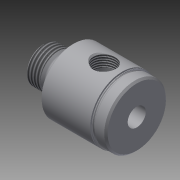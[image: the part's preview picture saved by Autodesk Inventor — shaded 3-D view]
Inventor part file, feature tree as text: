
AUTODESK INVENTOR PART (.ipt)
format: ipt  version: 2014 SP2 (Build 180246200, 246)  size: 267,776 bytes
history: native  units: in
note: dims shown in document units (in); Inventor stores cm internally (conversion verified against a paired STEP export)
features: other x119, sketch x5, revolve x4, thread x2, hole x1
ambient origin geometry x8: Origin, YZ Plane, XZ Plane, XY Plane, X Axis, Y Axis, Z Axis, Center Point
bodies: Solid1 (feature_tree)
feature tree (131):
  revolve  "Revolution1"  [1 undecoded]
  thread  "Thread1"  [1 undecoded]
  revolve  "Revolution2"  Angle=360.0deg
  hole  "Hole1"  [1 undecoded]
  revolve  "Revolution3"  [1 undecoded]
  thread  "Thread2"  [1 undecoded]
  revolve  "Revolution4"  [1 undecoded]
  other  "dp1_XY"
  other  "dp1_YZ"
  other  "dp1_ZX"
  other  "dp1_X"
  other  "dp1_Y"
  other  "dp1_Z"
  other  "dp1_Center"
  other  "dp2_XY"
  other  "dp2_YZ"
  other  "dp2_ZX"
  other  "dp2_X"
  other  "dp2_Y"
  other  "dp2_Z"
  other  "dp2_Center"
  other  "hh_XY"
  other  "hh_YZ"
  other  "hh_ZX"
  other  "hh_X"
  other  "hh_Y"
  other  "hh_Z"
  other  "hh_Center"
  other  "port_XY"
  other  "port_YZ"
  other  "port_ZX"
  other  "port_X"
  other  "port_Y"
  other  "port_Z"
  other  "port_Center"
  other  "rod_guide_XY"
  other  "rod_guide_YZ"
  other  "rod_guide_ZX"
  other  "rod_guide_X"
  other  "rod_guide_Y"
  other  "rod_guide_Z"
  other  "rod_guide_Center"
  other  "s1_XY"
  other  "s1_YZ"
  other  "s1_ZX"
  other  "s1_X"
  other  "s1_Y"
  other  "s1_Z"
  other  "s1_Center"
  other  "s2_XY"
  other  "s2_YZ"
  other  "s2_ZX"
  other  "s2_X"
  other  "s2_Y"
  other  "s2_Z"
  other  "s2_Center"
  other  "t1_XY"
  other  "t1_YZ"
  other  "t1_ZX"
  other  "t1_X"
  other  "t1_Y"
  other  "t1_Z"
  other  "t1_Center"
  other  "t111_XY"
  other  "t111_YZ"
  other  "t111_ZX"
  other  "t111_X"
  other  "t111_Y"
  other  "t111_Z"
  other  "t111_Center"
  other  "to_foot_bracket_XY"
  other  "to_foot_bracket_YZ"
  other  "to_foot_bracket_ZX"
  other  "to_foot_bracket_X"
  other  "to_foot_bracket_Y"
  other  "to_foot_bracket_Z"
  other  "to_foot_bracket_Center"
  other  "to_nut_XY"
  other  "to_nut_YZ"
  other  "to_nut_ZX"
  other  "to_nut_X"
  other  "to_nut_Y"
  other  "to_nut_Z"
  other  "to_nut_Center"
  other  "to_rod_XY"
  other  "to_rod_YZ"
  other  "to_rod_ZX"
  other  "to_rod_X"
  other  "to_rod_Y"
  other  "to_rod_Z"
  other  "to_rod_Center"
  other  "to_screw_XY"
  other  "to_screw_YZ"
  other  "to_screw_ZX"
  other  "to_screw_X"
  other  "to_screw_Y"
  other  "to_screw_Z"
  other  "to_screw_Center"
  other  "to_trunnion_brackets_XY"
  other  "to_trunnion_brackets_YZ"
  other  "to_trunnion_brackets_ZX"
  other  "to_trunnion_brackets_X"
  other  "to_trunnion_brackets_Y"
  other  "to_trunnion_brackets_Z"
  other  "to_trunnion_brackets_Center"
  other  "to_trunnion_brackets1_XY"
  other  "to_trunnion_brackets1_YZ"
  other  "to_trunnion_brackets1_ZX"
  other  "to_trunnion_brackets1_X"
  other  "to_trunnion_brackets1_Y"
  other  "to_trunnion_brackets1_Z"
  other  "to_trunnion_brackets1_Center"
  other  "to_trunnion_brackets2_XY"
  other  "to_trunnion_brackets2_YZ"
  other  "to_trunnion_brackets2_ZX"
  other  "to_trunnion_brackets2_X"
  other  "to_trunnion_brackets2_Y"
  other  "to_trunnion_brackets2_Z"
  other  "to_trunnion_brackets2_Center"
  other  "to_tube_XY"
  other  "to_tube_YZ"
  other  "to_tube_ZX"
  other  "to_tube_X"
  other  "to_tube_Y"
  other  "to_tube_Z"
  other  "to_tube_Center"
  sketch  "Sketch_2"  dims[d0=360.0deg d1=0.2297in d2=0.0in d3=360.0deg]
  sketch  "Sketch_3"  dims[d4=0.316in d5=0.75in d6=0.376in d7=0.25in d8=90.0deg d9=1.625in d10=0.0in d11=360.0deg]
  sketch  "Sketch3"  dims[d12=0.2001in d13=0.0in d14=360.0deg]
  sketch  "Sketch_43"  dims[d15=0.0in d16=0.0in d17=0.0in d18=0.0in d19=0.0in d20=0.0in]
  sketch  "Sketch_47"
note: 6 required parameter values undecoded (feature->parameter linkage not recoverable at this tier; creation-order binding heuristic only, values carry confidence <= 0.55)